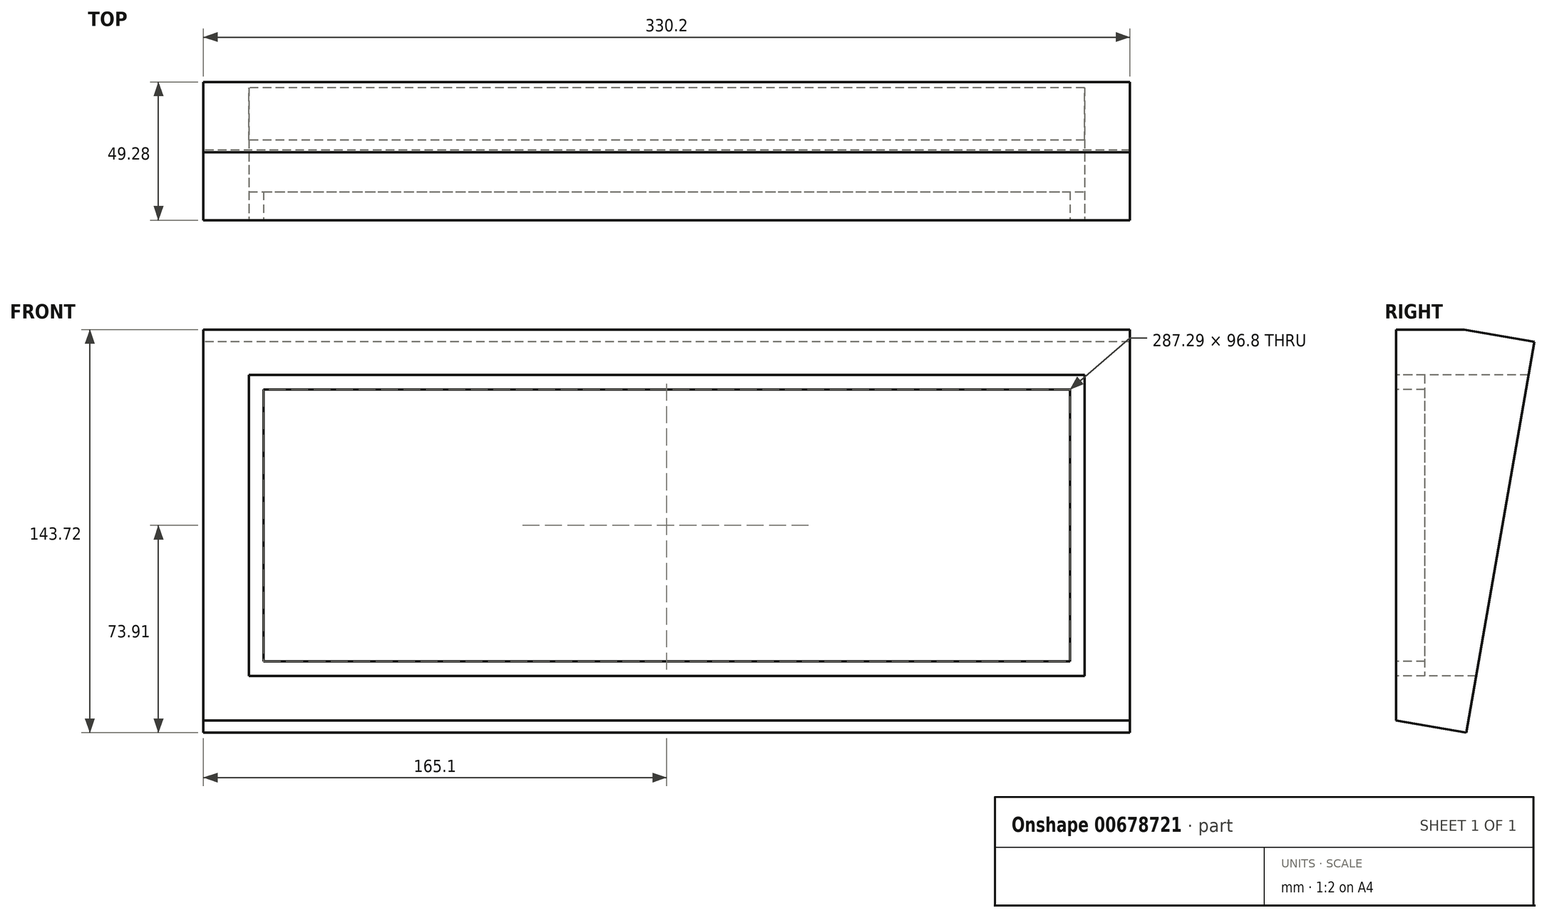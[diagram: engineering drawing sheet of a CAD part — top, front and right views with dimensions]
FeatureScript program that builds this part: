
annotation { "Feature Type Name" : "Feature", "Feature Type Description" : "" }
export const myFeature = defineFeature(function(context is Context, id is Id, definition is map)
    precondition{}
    {
        {
            var Q0;
            Q0=qCreatedBy(makeId("Front.planeOp"),FACE);
            var sketch = newSketch(context, id + "F0", { "sketchPlane" : qUnion([Q0])});
            skLineSegment(sketch, "E0.bottom", {"start": v(-143.64, 48.4) * mm, "end": v(143.64, 48.4) * mm});
            skLineSegment(sketch, "E0.top", {"start": v(-143.64, -48.4) * mm, "end": v(143.64, -48.4) * mm});
            skLineSegment(sketch, "E0.left", {"start": v(-143.64, 48.4) * mm, "end": v(-143.64, -48.4) * mm});
            skLineSegment(sketch, "E0.right", {"start": v(143.64, 48.4) * mm, "end": v(143.64, -48.4) * mm});
            skPoint(sketch, "E0.middle", {"position": v(0, 0) * mm});
            skLineSegment(sketch, "E1.bottom", {"start": v(-148.88, 53.63) * mm, "end": v(148.88, 53.63) * mm});
            skLineSegment(sketch, "E1.top", {"start": v(-148.88, -53.63) * mm, "end": v(148.88, -53.63) * mm});
            skLineSegment(sketch, "E1.left", {"start": v(-148.88, 53.63) * mm, "end": v(-148.88, -53.63) * mm});
            skLineSegment(sketch, "E1.right", {"start": v(148.88, 53.63) * mm, "end": v(148.88, -53.63) * mm});
            skLineSegment(sketch, "E2.bottom", {"start": v(-165.1, 69.85) * mm, "end": v(165.1, 69.85) * mm});
            skLineSegment(sketch, "E2.top", {"start": v(-165.1, -69.85) * mm, "end": v(165.1, -69.85) * mm});
            skLineSegment(sketch, "E2.left", {"start": v(-165.1, 69.85) * mm, "end": v(-165.1, -69.85) * mm});
            skLineSegment(sketch, "E2.right", {"start": v(165.1, 69.85) * mm, "end": v(165.1, -69.85) * mm});
            skSolve(sketch);
        }
        {
            var Q0;
            Q0=qCreatedBy(makeId("Right.planeOp"),FACE);
            var sketch = newSketch(context, id + "F1", { "sketchPlane" : qUnion([Q0])});
            skLineSegment(sketch, "E3", {"start": v(0, -69.55) * mm, "end": v(24.26, 69.8) * mm});
            skLineSegment(sketch, "E4", {"start": v(24.26, 69.8) * mm, "end": v(0, 69.75) * mm});
            skLineSegment(sketch, "E5", {"start": v(0, 69.75) * mm, "end": v(0, -69.55) * mm});
            skSolve(sketch);
        }
        {
            var Q0;
            Q0=makeQuery(id+"F1.imprint","IMPRINT",FACE,{"disambiguationData":[TD([[makeQuery(id+"F1.imprint","IMPRINT",EDGE,{"derivedFrom":sQuery(id+"F1.wireOp",EDGE,"E3")}),1.0]])]});
            extrude(context, id + "F2", {"entities" : qUnion([Q0]), "depth" : 165.1 * mm, "offsetDistance" : 25.4 * mm, "hasSecondDirection" : true, "secondDirectionOppositeDirection" : true, "secondDirectionDepth" : 165.1 * mm});
        }
        {
            var Q0;
            Q0=makeQuery(id+"F2.opExtrude","SWEPT_FACE",FACE,{"disambiguationData":[OSD([sQuery(id+"F1.wireOp",EDGE,"E3")])]});
            var sketch = newSketch(context, id + "F3", { "sketchPlane" : qUnion([Q0])});
            skLineSegment(sketch, "E6", {"start": v(-165.1, 72.93) * mm, "end": v(-165.1, -68.52) * mm});
            skLineSegment(sketch, "E7", {"start": v(-165.1, -68.52) * mm, "end": v(165.1, -68.52) * mm});
            skLineSegment(sketch, "E8", {"start": v(165.1, -68.52) * mm, "end": v(165.1, 72.93) * mm});
            skLineSegment(sketch, "E9", {"start": v(165.1, 72.93) * mm, "end": v(-165.1, 72.93) * mm});
            skSolve(sketch);
        }
        {
            var Q0;
            Q0=makeQuery(id+"F3.imprint","IMPRINT",FACE,{"disambiguationData":[TD([[makeQuery(id+"F3.imprint","IMPRINT",EDGE,{"derivedFrom":sQuery(id+"F3.wireOp",EDGE,"E6")}),-1.0]])]});
            extrude(context, id + "F4", {"entities" : qUnion([Q0]), "operationType" : NewBodyOperationType.ADD, "depth" : 25.4 * mm, "offsetDistance" : 25.4 * mm});
        }
        {
            var Q0;
            Q0=makeQuery(id+"F0.imprint","IMPRINT",FACE,{"disambiguationData":[TD([[makeQuery(id+"F0.imprint","IMPRINT",EDGE,{"derivedFrom":sQuery(id+"F0.wireOp",EDGE,"E0.bottom")}),1.0]])]});
            extrude(context, id + "F5", {"entities" : qUnion([Q0]), "operationType" : NewBodyOperationType.REMOVE, "endBound" : BoundingType.THROUGH_ALL, "oppositeDirection" : true, "depth" : 5.08 * mm, "offsetDistance" : 25.4 * mm});
        }
        {
            var Q0;
            Q0=makeQuery(id+"F0.imprint","IMPRINT",FACE,{"disambiguationData":[TD([[makeQuery(id+"F0.imprint","IMPRINT",EDGE,{"derivedFrom":sQuery(id+"F0.wireOp",EDGE,"E0.bottom")}),1.0]])]});
            extrude(context, id + "F6", {"entities" : qUnion([Q0]), "oppositeDirection" : true, "depth" : 10.16 * mm, "offsetDistance" : 25.4 * mm});
        }
        {
            var Q0;
            Q0=makeQuery(id+"F0.imprint","IMPRINT",FACE,{"disambiguationData":[TD([[makeQuery(id+"F0.imprint","IMPRINT",EDGE,{"derivedFrom":sQuery(id+"F0.wireOp",EDGE,"E0.bottom")}),-1.0]])]});
            extrude(context, id + "F7", {"entities" : qUnion([Q0]), "operationType" : NewBodyOperationType.REMOVE, "endBound" : BoundingType.THROUGH_ALL, "oppositeDirection" : true, "depth" : 25.4 * mm, "offsetDistance" : 25.4 * mm});
        }
    });
